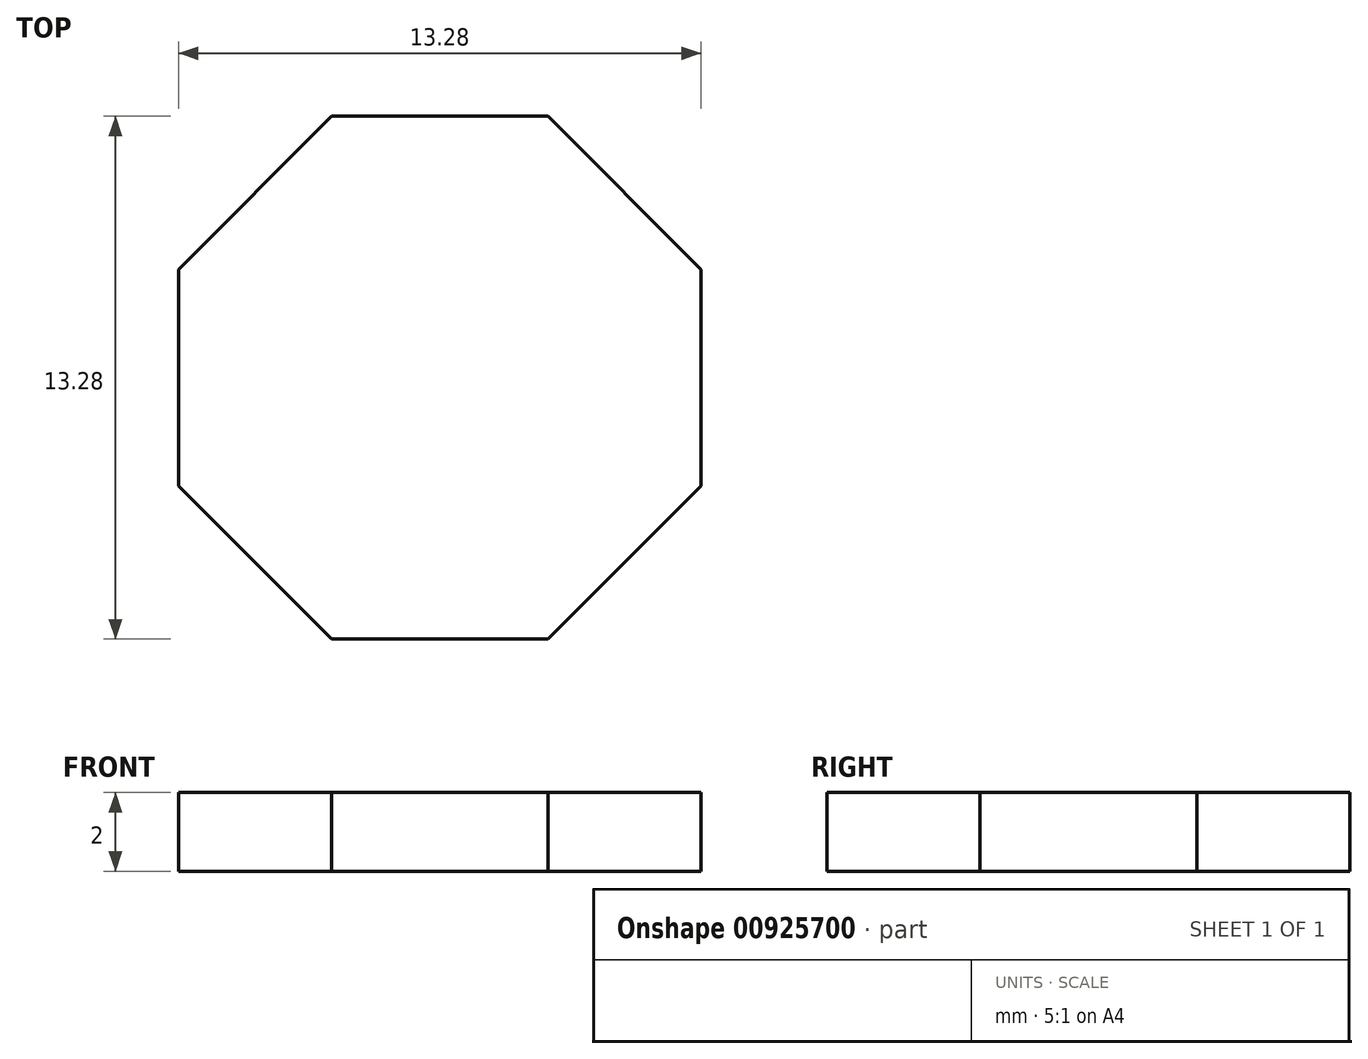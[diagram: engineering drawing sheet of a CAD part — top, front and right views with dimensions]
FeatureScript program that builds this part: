
annotation { "Feature Type Name" : "Feature", "Feature Type Description" : "" }
export const myFeature = defineFeature(function(context is Context, id is Id, definition is map)
    precondition{}
    {
        {
            var Q0;
            Q0=qCreatedBy(makeId("Top.planeOp"),FACE);
            var sketch = newSketch(context, id + "F0", { "sketchPlane" : qUnion([Q0])});
            skCircle(sketch, "E0.cCircle", {"center": v(0, 0) * mm, "radius": 6.64 * mm, "construction": true});
            skLineSegment(sketch, "E0.0", {"start": v(6.64, 2.75) * mm, "end": v(6.64, -2.75) * mm});
            skLineSegment(sketch, "E0.1", {"start": v(6.64, -2.75) * mm, "end": v(2.75, -6.64) * mm});
            skLineSegment(sketch, "E0.2", {"start": v(2.75, -6.64) * mm, "end": v(-2.75, -6.64) * mm});
            skLineSegment(sketch, "E0.3", {"start": v(-2.75, -6.64) * mm, "end": v(-6.64, -2.75) * mm});
            skLineSegment(sketch, "E0.4", {"start": v(-6.64, -2.75) * mm, "end": v(-6.64, 2.75) * mm});
            skLineSegment(sketch, "E0.5", {"start": v(-6.64, 2.75) * mm, "end": v(-2.75, 6.64) * mm});
            skLineSegment(sketch, "E0.6", {"start": v(-2.75, 6.64) * mm, "end": v(2.75, 6.64) * mm});
            skLineSegment(sketch, "E0.7", {"start": v(2.75, 6.64) * mm, "end": v(6.64, 2.75) * mm});
            skPoint(sketch, "E0.0.midPoint", {"position": v(6.64, 0) * mm});
            skSolve(sketch);
        }
        {
            var Q0;
            Q0=makeQuery(id+"F0.imprint","IMPRINT",FACE,{"disambiguationData":[TD([[makeQuery(id+"F0.imprint","IMPRINT",EDGE,{"derivedFrom":sQuery(id+"F0.wireOp",EDGE,"E0.0")}),-1.0]])]});
            extrude(context, id + "F1", {"entities" : qUnion([Q0]), "depth" : 2 * mm, "offsetDistance" : 25 * mm});
        }
    });
